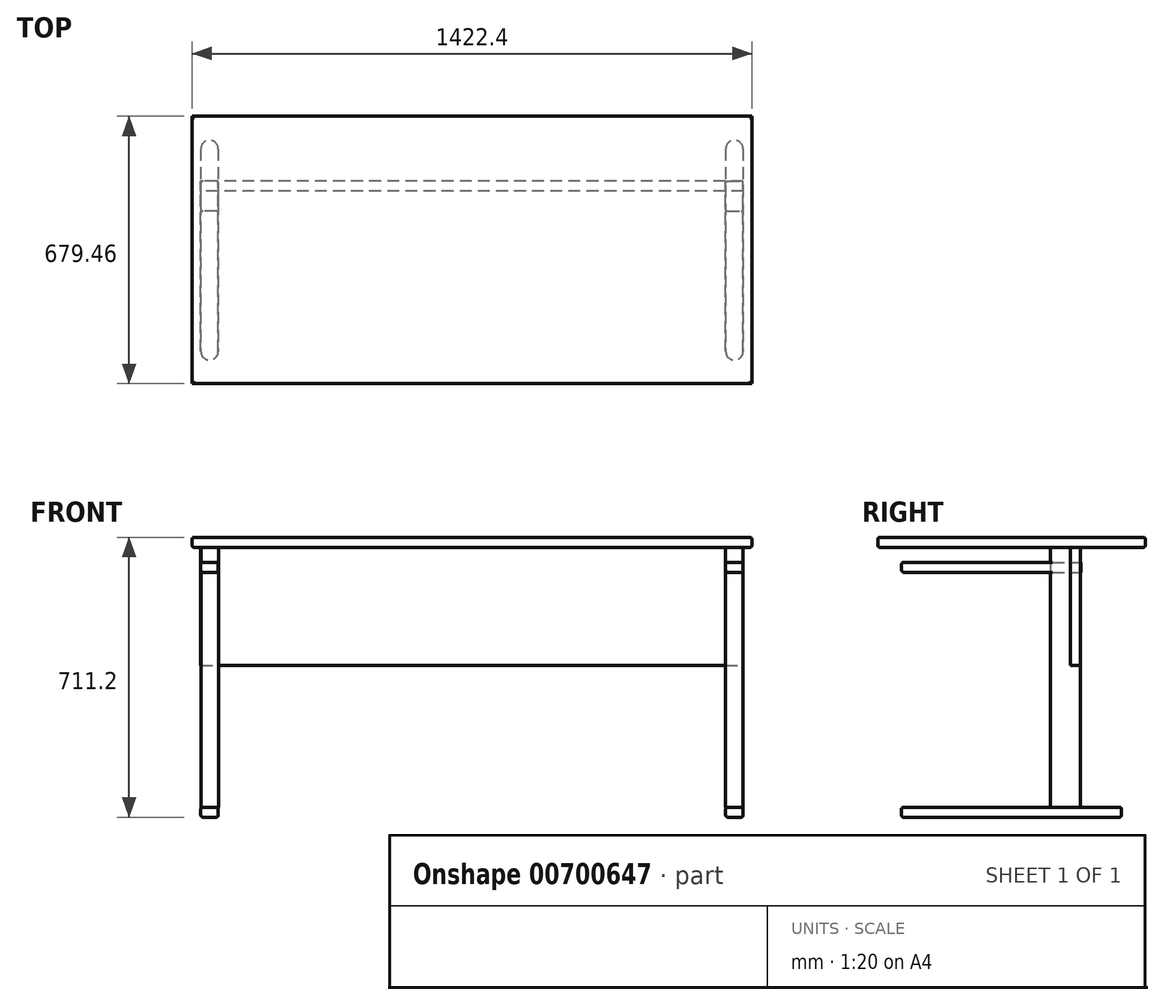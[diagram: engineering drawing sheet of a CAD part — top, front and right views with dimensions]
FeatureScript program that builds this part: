
annotation { "Feature Type Name" : "Feature", "Feature Type Description" : "" }
export const myFeature = defineFeature(function(context is Context, id is Id, definition is map)
    precondition{}
    {
        {
            var Q0;
            Q0=qCreatedBy(makeId("Top.planeOp"),FACE);
            var sketch = newSketch(context, id + "F0", { "sketchPlane" : qUnion([Q0])});
            skLineSegment(sketch, "E0", {"start": v(0, 0) * mm, "end": v(644.52, 0) * mm, "construction": true});
            skArc(sketch, "E1", {"start": v(688.98, 256.73) * mm, "mid": v(666.75, 278.95) * mm, "end": v(644.52, 256.73) * mm});
            skLineSegment(sketch, "E2", {"start": v(688.98, 256.73) * mm, "end": v(688.98, -257.62) * mm});
            skLineSegment(sketch, "E3", {"start": v(644.52, 256.73) * mm, "end": v(644.52, -257.62) * mm});
            skArc(sketch, "E4", {"start": v(644.52, -257.62) * mm, "mid": v(666.75, -279.85) * mm, "end": v(688.98, -257.62) * mm});
            skArc(sketch, "E5.MirrorCS", {"start": v(-644.52, -257.62) * mm, "mid": v(-666.75, -279.85) * mm, "end": v(-688.98, -257.62) * mm});
            skArc(sketch, "E6.MirrorCS", {"start": v(-688.98, 256.73) * mm, "mid": v(-666.75, 278.95) * mm, "end": v(-644.52, 256.73) * mm});
            skLineSegment(sketch, "E7.MirrorCS", {"start": v(-644.52, 256.73) * mm, "end": v(-644.52, -257.62) * mm});
            skLineSegment(sketch, "E8.MirrorCS", {"start": v(-688.98, 256.73) * mm, "end": v(-688.98, -257.62) * mm});
            skSolve(sketch);
        }
        {
            var Q0;
            Q0 = qSketchRegion(id + "F0", true);
            extrude(context, id + "F1", {"entities" : qUnion([Q0]), "depth" : 25.4 * mm, "offsetDistance" : 25.4 * mm});
        }
        {
            var Q0;
            Q0=makeQuery(id+"F1.opExtrude","CAP_FACE",FACE,{"disambiguationData":[OSD([sQuery(id+"F0.wireOp",EDGE,"E5.MirrorCS"),sQuery(id+"F0.wireOp",EDGE,"E6.MirrorCS"),sQuery(id+"F0.wireOp",EDGE,"E7.MirrorCS"),sQuery(id+"F0.wireOp",EDGE,"E8.MirrorCS")])],"isStart":false});
            cPlane(context, id + "F2", {"entities" : qUnion([Q0]), "cplaneType" : CPlaneType.OFFSET, "offset" : 0 * mm, "width" : 152.4 * mm, "height" : 152.4 * mm});
        }
        {
            var Q0;
            Q0=qCreatedBy(id+"F2.planeOp",FACE);
            var sketch = newSketch(context, id + "F3", { "sketchPlane" : qUnion([Q0])});
            skLineSegment(sketch, "E9", {"start": v(0, 0) * mm, "end": v(0, 98.43) * mm, "construction": true});
            skLineSegment(sketch, "E10", {"start": v(0, 98.43) * mm, "end": v(644.36, 98.43) * mm, "construction": true});
            skLineSegment(sketch, "E11.bottom", {"start": v(644.36, 98.43) * mm, "end": v(688.8, 98.43) * mm});
            skLineSegment(sketch, "E11.top", {"start": v(644.36, 174.63) * mm, "end": v(688.8, 174.63) * mm});
            skLineSegment(sketch, "E11.left", {"start": v(644.36, 98.43) * mm, "end": v(644.36, 174.63) * mm});
            skLineSegment(sketch, "E11.right", {"start": v(688.8, 98.43) * mm, "end": v(688.8, 174.63) * mm});
            skLineSegment(sketch, "E12.MirrorCS", {"start": v(-644.36, 174.63) * mm, "end": v(-688.8, 174.63) * mm});
            skLineSegment(sketch, "E13.MirrorCS", {"start": v(-644.36, 98.43) * mm, "end": v(-688.8, 98.43) * mm});
            skLineSegment(sketch, "E14.MirrorCS", {"start": v(-644.36, 98.43) * mm, "end": v(-644.36, 174.63) * mm});
            skLineSegment(sketch, "E15.MirrorCS", {"start": v(-688.8, 98.43) * mm, "end": v(-688.8, 174.63) * mm});
            skSolve(sketch);
        }
        {
            var Q0;
            Q0 = qSketchRegion(id + "F3", true);
            extrude(context, id + "F4", {"entities" : qUnion([Q0]), "depth" : 660.4 * mm, "offsetDistance" : 25.4 * mm});
        }
        {
            var Q0;
            Q0=makeQuery(id+"F4.opExtrude","SWEPT_FACE",FACE,{"disambiguationData":[OSD([sQuery(id+"F3.wireOp",EDGE,"E11.top")])]});
            cPlane(context, id + "F5", {"entities" : qUnion([Q0]), "cplaneType" : CPlaneType.OFFSET, "offset" : 0 * mm, "width" : 152.4 * mm, "height" : 152.4 * mm});
        }
        {
            var Q0;
            Q0=qCreatedBy(id+"F5.planeOp",FACE);
            var sketch = newSketch(context, id + "F6", { "sketchPlane" : qUnion([Q0])});
            skLineSegment(sketch, "E16", {"start": v(0, 0) * mm, "end": v(0, 386) * mm, "construction": true});
            skLineSegment(sketch, "E17.bottom", {"start": v(0, 685.8) * mm, "end": v(688.98, 685.8) * mm});
            skLineSegment(sketch, "E17.top", {"start": v(0, 386) * mm, "end": v(688.98, 386) * mm});
            skLineSegment(sketch, "E17.right", {"start": v(688.98, 685.8) * mm, "end": v(688.98, 386) * mm});
            skLineSegment(sketch, "E18.MirrorCS", {"start": v(0, 386) * mm, "end": v(-688.98, 386) * mm});
            skLineSegment(sketch, "E19.MirrorCS", {"start": v(0, 685.8) * mm, "end": v(-688.98, 685.8) * mm});
            skLineSegment(sketch, "E20.MirrorCS", {"start": v(-688.98, 685.8) * mm, "end": v(-688.98, 386) * mm});
            skSolve(sketch);
        }
        {
            var Q0;
            Q0 = qSketchRegion(id + "F6", true);
            extrude(context, id + "F7", {"entities" : qUnion([Q0]), "oppositeDirection" : true, "depth" : 25.4 * mm, "offsetDistance" : 25.4 * mm});
        }
        {
            var Q0;
            Q0=makeQuery(id+"F4.opExtrude","CAP_FACE",FACE,{"disambiguationData":[OSD([sQuery(id+"F3.wireOp",EDGE,"E12.MirrorCS"),sQuery(id+"F3.wireOp",EDGE,"E13.MirrorCS"),sQuery(id+"F3.wireOp",EDGE,"E14.MirrorCS"),sQuery(id+"F3.wireOp",EDGE,"E15.MirrorCS")])],"isStart":false});
            cPlane(context, id + "F8", {"entities" : qUnion([Q0]), "cplaneType" : CPlaneType.OFFSET, "offset" : 38.1 * mm, "oppositeDirection" : true, "width" : 152.4 * mm, "height" : 152.4 * mm});
        }
        {
            var Q0;
            Q0=qCreatedBy(id+"F8.planeOp",FACE);
            var sketch = newSketch(context, id + "F9", { "sketchPlane" : qUnion([Q0])});
            skLineSegment(sketch, "E21", {"start": v(0, 0) * mm, "end": v(-688.97, 0) * mm, "construction": true});
            skArc(sketch, "E22", {"start": v(-688.98, -257.18) * mm, "mid": v(-666.75, -279.4) * mm, "end": v(-644.53, -257.18) * mm});
            skLineSegment(sketch, "E23", {"start": v(-644.53, -257.18) * mm, "end": v(-644.53, 175.5) * mm});
            skLineSegment(sketch, "E24", {"start": v(-688.98, -257.18) * mm, "end": v(-688.98, 175.5) * mm});
            skLineSegment(sketch, "E25", {"start": v(-644.53, 175.5) * mm, "end": v(-688.98, 175.5) * mm});
            skLineSegment(sketch, "E26.MirrorCS", {"start": v(644.53, -257.18) * mm, "end": v(644.53, 175.5) * mm});
            skLineSegment(sketch, "E27.MirrorCS", {"start": v(0, 0) * mm, "end": v(688.97, 0) * mm, "construction": true});
            skLineSegment(sketch, "E28.MirrorCS", {"start": v(688.98, -257.18) * mm, "end": v(688.98, 175.5) * mm});
            skLineSegment(sketch, "E29.MirrorCS", {"start": v(644.53, 175.5) * mm, "end": v(688.98, 175.5) * mm});
            skArc(sketch, "E30.MirrorCS", {"start": v(688.98, -257.18) * mm, "mid": v(666.75, -279.4) * mm, "end": v(644.53, -257.18) * mm});
            skSolve(sketch);
        }
        {
            var Q0;
            Q0 = qSketchRegion(id + "F9", true);
            extrude(context, id + "F10", {"entities" : qUnion([Q0]), "oppositeDirection" : true, "depth" : 25.4 * mm, "offsetDistance" : 25.4 * mm});
        }
        {
            var Q0;
            Q0=makeQuery(id+"F4.opExtrude","CAP_FACE",FACE,{"disambiguationData":[OSD([sQuery(id+"F3.wireOp",EDGE,"E12.MirrorCS"),sQuery(id+"F3.wireOp",EDGE,"E13.MirrorCS"),sQuery(id+"F3.wireOp",EDGE,"E14.MirrorCS"),sQuery(id+"F3.wireOp",EDGE,"E15.MirrorCS")])],"isStart":false});
            cPlane(context, id + "F11", {"entities" : qUnion([Q0]), "cplaneType" : CPlaneType.OFFSET, "offset" : 0 * mm, "width" : 152.4 * mm, "height" : 152.4 * mm});
        }
        {
            var Q0;
            Q0=qCreatedBy(id+"F11.planeOp",FACE);
            var sketch = newSketch(context, id + "F12", { "sketchPlane" : qUnion([Q0])});
            skLineSegment(sketch, "E31.bottom", {"start": v(711.2, 339.73) * mm, "end": v(-711.2, 339.73) * mm});
            skLineSegment(sketch, "E31.top", {"start": v(711.2, -339.73) * mm, "end": v(-711.2, -339.73) * mm});
            skLineSegment(sketch, "E31.left", {"start": v(711.2, 339.73) * mm, "end": v(711.2, -339.73) * mm});
            skLineSegment(sketch, "E31.right", {"start": v(-711.2, 339.73) * mm, "end": v(-711.2, -339.73) * mm});
            skPoint(sketch, "E31.middle", {"position": v(0, 0) * mm});
            skSolve(sketch);
        }
        {
            var Q0;
            Q0 = qSketchRegion(id + "F12", true);
            extrude(context, id + "F13", {"entities" : qUnion([Q0]), "depth" : 25.4 * mm, "offsetDistance" : 25.4 * mm});
        }
        {
            var Q0;
            Q0=makeQuery(id+"F4.opExtrude","SWEPT_EDGE",EDGE,{"disambiguationData":[OSD([sQuery(id+"F3.wireOp",EDGE,"E12.MirrorCS"),sQuery(id+"F3.wireOp",EDGE,"E15.MirrorCS")])]});
            var Q1;
            Q1=makeQuery(id+"F4.opExtrude","SWEPT_EDGE",EDGE,{"disambiguationData":[OSD([sQuery(id+"F3.wireOp",EDGE,"E11.top"),sQuery(id+"F3.wireOp",EDGE,"E11.left")])]});
            var Q2;
            Q2=makeQuery(id+"F4.opExtrude","SWEPT_EDGE",EDGE,{"disambiguationData":[OSD([sQuery(id+"F3.wireOp",EDGE,"E11.top"),sQuery(id+"F3.wireOp",EDGE,"E11.right")])]});
            var Q3;
            Q3=makeQuery(id+"F4.opExtrude","SWEPT_EDGE",EDGE,{"disambiguationData":[OSD([sQuery(id+"F3.wireOp",EDGE,"E12.MirrorCS"),sQuery(id+"F3.wireOp",EDGE,"E14.MirrorCS")])]});
            var Q4;
            Q4=makeQuery(id+"F4.opExtrude","SWEPT_EDGE",EDGE,{"disambiguationData":[OSD([sQuery(id+"F3.wireOp",EDGE,"E13.MirrorCS"),sQuery(id+"F3.wireOp",EDGE,"E14.MirrorCS")])]});
            var Q5;
            Q5=makeQuery(id+"F4.opExtrude","SWEPT_EDGE",EDGE,{"disambiguationData":[OSD([sQuery(id+"F3.wireOp",EDGE,"E13.MirrorCS"),sQuery(id+"F3.wireOp",EDGE,"E15.MirrorCS")])]});
            var Q6;
            Q6=makeQuery(id+"F4.opExtrude","SWEPT_EDGE",EDGE,{"disambiguationData":[OSD([sQuery(id+"F3.wireOp",EDGE,"E11.bottom"),sQuery(id+"F3.wireOp",EDGE,"E11.right")])]});
            var Q7;
            Q7=makeQuery(id+"F4.opExtrude","SWEPT_EDGE",EDGE,{"disambiguationData":[OSD([sQuery(id+"F3.wireOp",EDGE,"E11.bottom"),sQuery(id+"F3.wireOp",EDGE,"E11.left")])]});
            fillet(context, id + "F14", {"entities" : qUnion([Q0, Q1, Q2, Q3, Q4, Q5, Q6, Q7]), "radius" : 5.08 * mm, "tangentPropagation" : true, "allowEdgeOverflow" : false});
        }
        {
            var Q0;
            Q0=makeQuery(id+"F1.opExtrude","CAP_EDGE",EDGE,{"disambiguationData":[OSD([sQuery(id+"F0.wireOp",EDGE,"E7.MirrorCS")])],"isStart":false});
            var Q1;
            Q1=makeQuery(id+"F1.opExtrude","CAP_EDGE",EDGE,{"disambiguationData":[OSD([sQuery(id+"F0.wireOp",EDGE,"E7.MirrorCS")])],"isStart":true});
            var Q2;
            Q2=makeQuery(id+"F1.opExtrude","CAP_EDGE",EDGE,{"disambiguationData":[OSD([sQuery(id+"F0.wireOp",EDGE,"E8.MirrorCS")])],"isStart":false});
            var Q3;
            Q3=makeQuery(id+"F1.opExtrude","CAP_EDGE",EDGE,{"disambiguationData":[OSD([sQuery(id+"F0.wireOp",EDGE,"E2")])],"isStart":false});
            var Q4;
            Q4=makeQuery(id+"F1.opExtrude","CAP_EDGE",EDGE,{"disambiguationData":[OSD([sQuery(id+"F0.wireOp",EDGE,"E2")])],"isStart":true});
            var Q5;
            Q5=makeQuery(id+"F1.opExtrude","CAP_EDGE",EDGE,{"disambiguationData":[OSD([sQuery(id+"F0.wireOp",EDGE,"E8.MirrorCS")])],"isStart":true});
            var Q6;
            Q6=makeQuery(id+"F1.opExtrude","CAP_EDGE",EDGE,{"disambiguationData":[OSD([sQuery(id+"F0.wireOp",EDGE,"E3")])],"isStart":false});
            var Q7;
            Q7=makeQuery(id+"F1.opExtrude","CAP_EDGE",EDGE,{"disambiguationData":[OSD([sQuery(id+"F0.wireOp",EDGE,"E3")])],"isStart":true});
            var Q8;
            Q8=makeQuery(id+"F10.opExtrude","CAP_EDGE",EDGE,{"disambiguationData":[OSD([sQuery(id+"F9.wireOp",EDGE,"E24")])],"isStart":true});
            var Q9;
            Q9=makeQuery(id+"F10.opExtrude","CAP_EDGE",EDGE,{"disambiguationData":[OSD([sQuery(id+"F9.wireOp",EDGE,"E24")])],"isStart":false});
            var Q10;
            Q10=makeQuery(id+"F10.opExtrude","CAP_EDGE",EDGE,{"disambiguationData":[OSD([sQuery(id+"F9.wireOp",EDGE,"E23")])],"isStart":true});
            var Q11;
            Q11=makeQuery(id+"F10.opExtrude","CAP_EDGE",EDGE,{"disambiguationData":[OSD([sQuery(id+"F9.wireOp",EDGE,"E23")])],"isStart":false});
            var Q12;
            Q12=makeQuery(id+"F10.opExtrude","CAP_EDGE",EDGE,{"disambiguationData":[OSD([sQuery(id+"F9.wireOp",EDGE,"E22")])],"isStart":true});
            var Q13;
            Q13=makeQuery(id+"F10.opExtrude","CAP_EDGE",EDGE,{"disambiguationData":[OSD([sQuery(id+"F9.wireOp",EDGE,"E22")])],"isStart":false});
            var Q14;
            Q14=makeQuery(id+"F1.opExtrude","CAP_EDGE",EDGE,{"disambiguationData":[OSD([sQuery(id+"F0.wireOp",EDGE,"E5.MirrorCS")])],"isStart":false});
            var Q15;
            Q15=makeQuery(id+"F1.opExtrude","CAP_EDGE",EDGE,{"disambiguationData":[OSD([sQuery(id+"F0.wireOp",EDGE,"E4")])],"isStart":false});
            var Q16;
            Q16=makeQuery(id+"F1.opExtrude","CAP_EDGE",EDGE,{"disambiguationData":[OSD([sQuery(id+"F0.wireOp",EDGE,"E4")])],"isStart":true});
            var Q17;
            Q17=makeQuery(id+"F1.opExtrude","CAP_EDGE",EDGE,{"disambiguationData":[OSD([sQuery(id+"F0.wireOp",EDGE,"E5.MirrorCS")])],"isStart":true});
            var Q18;
            Q18=makeQuery(id+"F10.opExtrude","CAP_EDGE",EDGE,{"disambiguationData":[OSD([sQuery(id+"F9.wireOp",EDGE,"E28.MirrorCS")])],"isStart":true});
            var Q19;
            Q19=makeQuery(id+"F10.opExtrude","CAP_EDGE",EDGE,{"disambiguationData":[OSD([sQuery(id+"F9.wireOp",EDGE,"E28.MirrorCS")])],"isStart":false});
            var Q20;
            Q20=makeQuery(id+"F10.opExtrude","CAP_EDGE",EDGE,{"disambiguationData":[OSD([sQuery(id+"F9.wireOp",EDGE,"E30.MirrorCS")])],"isStart":true});
            var Q21;
            Q21=makeQuery(id+"F10.opExtrude","CAP_EDGE",EDGE,{"disambiguationData":[OSD([sQuery(id+"F9.wireOp",EDGE,"E30.MirrorCS")])],"isStart":false});
            var Q22;
            Q22=makeQuery(id+"F10.opExtrude","CAP_EDGE",EDGE,{"disambiguationData":[OSD([sQuery(id+"F9.wireOp",EDGE,"E26.MirrorCS")])],"isStart":true});
            var Q23;
            Q23=makeQuery(id+"F10.opExtrude","CAP_EDGE",EDGE,{"disambiguationData":[OSD([sQuery(id+"F9.wireOp",EDGE,"E26.MirrorCS")])],"isStart":false});
            fillet(context, id + "F15", {"entities" : qUnion([Q0, Q1, Q2, Q3, Q4, Q5, Q6, Q7, Q8, Q9, Q10, Q11, Q12, Q13, Q14, Q15, Q16, Q17, Q18, Q19, Q20, Q21, Q22, Q23]), "radius" : 5.08 * mm, "tangentPropagation" : true, "allowEdgeOverflow" : false});
        }
        {
            var Q0;
            Q0=makeQuery(id+"F13.opExtrude","CAP_FACE",FACE,{"disambiguationData":[OSD([sQuery(id+"F12.wireOp",EDGE,"E31.bottom"),sQuery(id+"F12.wireOp",EDGE,"E31.top"),sQuery(id+"F12.wireOp",EDGE,"E31.left"),sQuery(id+"F12.wireOp",EDGE,"E31.right")])],"isStart":false});
            var Q1;
            Q1=makeQuery(id+"F13.opExtrude","CAP_FACE",FACE,{"disambiguationData":[OSD([sQuery(id+"F12.wireOp",EDGE,"E31.bottom"),sQuery(id+"F12.wireOp",EDGE,"E31.top"),sQuery(id+"F12.wireOp",EDGE,"E31.left"),sQuery(id+"F12.wireOp",EDGE,"E31.right")])],"isStart":true});
            fillet(context, id + "F16", {"entities" : qUnion([Q0, Q1]), "radius" : 5.08 * mm, "tangentPropagation" : true, "allowEdgeOverflow" : false});
        }
    });
